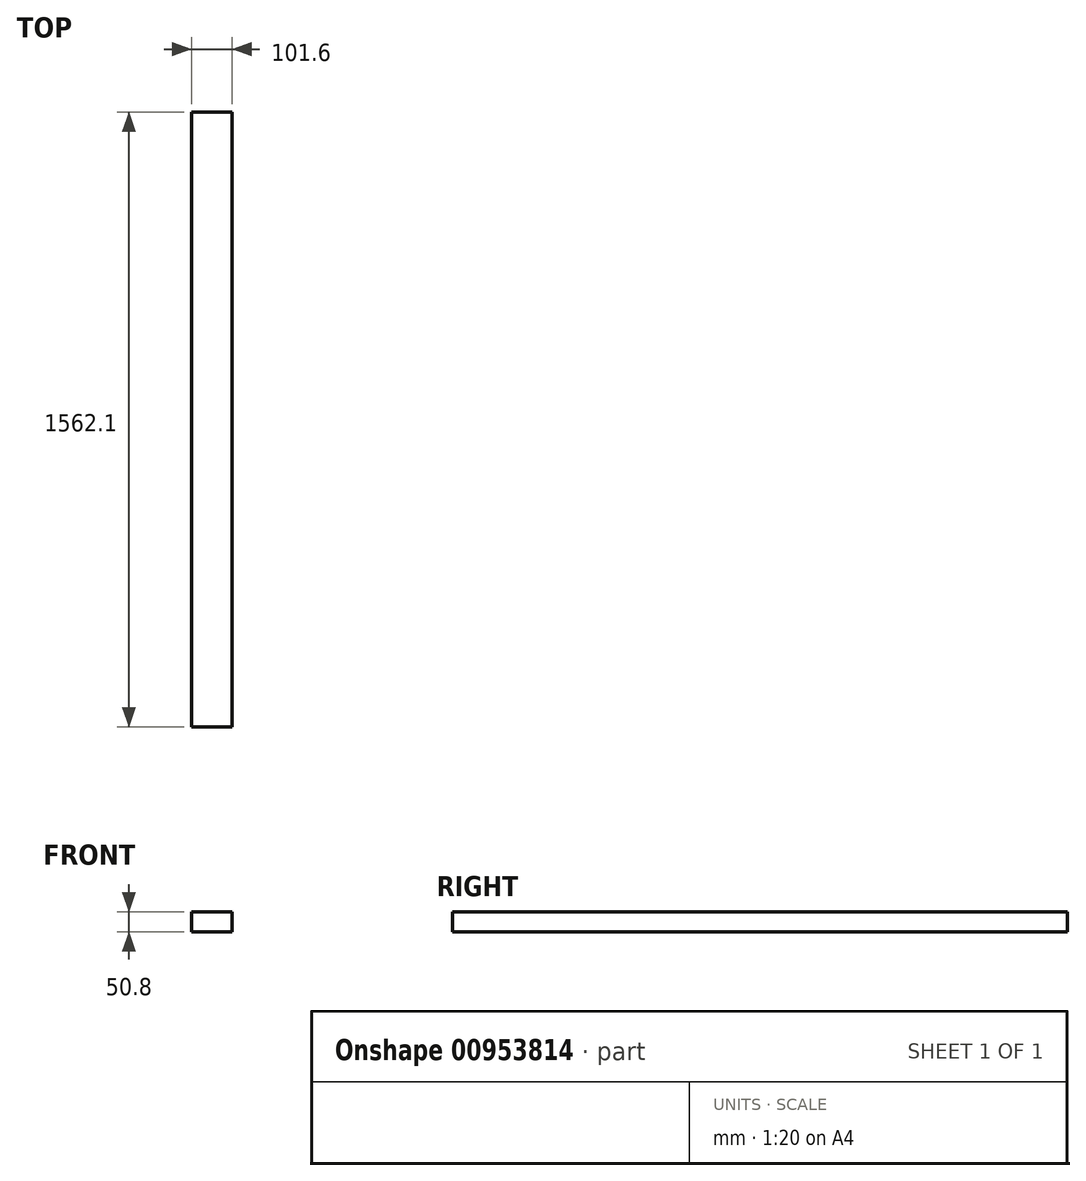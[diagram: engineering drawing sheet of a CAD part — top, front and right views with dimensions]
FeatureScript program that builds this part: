
annotation { "Feature Type Name" : "Feature", "Feature Type Description" : "" }
export const myFeature = defineFeature(function(context is Context, id is Id, definition is map)
    precondition{}
    {
        {
            var Q0;
            Q0=qCreatedBy(makeId("Front.planeOp"),FACE);
            var sketch = newSketch(context, id + "F0", { "sketchPlane" : qUnion([Q0])});
            skLineSegment(sketch, "E0.bottom", {"start": v(-50.8, -25.4) * mm, "end": v(50.8, -25.4) * mm});
            skLineSegment(sketch, "E0.top", {"start": v(-50.8, 25.4) * mm, "end": v(50.8, 25.4) * mm});
            skLineSegment(sketch, "E0.left", {"start": v(-50.8, -25.4) * mm, "end": v(-50.8, 25.4) * mm});
            skLineSegment(sketch, "E0.right", {"start": v(50.8, -25.4) * mm, "end": v(50.8, 25.4) * mm});
            skPoint(sketch, "E0.middle", {"position": v(0, 0) * mm});
            skSolve(sketch);
        }
        {
            var Q0;
            Q0 = qSketchRegion(id + "F0", true);
            extrude(context, id + "F1", {"entities" : qUnion([Q0]), "depth" : 1562.1 * mm, "offsetDistance" : 25.4 * mm});
        }
    });
